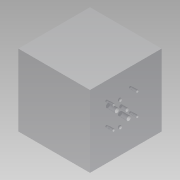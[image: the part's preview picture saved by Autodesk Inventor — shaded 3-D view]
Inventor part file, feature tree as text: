
AUTODESK INVENTOR PART (.ipt)
format: ipt  version: 2014 (Build 180170000, 170)  size: 202,240 bytes
history: native  units: mm
features: other x48, extrude x16, sketch x16
ambient origin geometry x8: Origin, YZ Plane, XZ Plane, XY Plane, X Axis, Y Axis, Z Axis, Center Point
bodies: 实体1 (feature_tree)
feature tree (80):
  extrude  "拉伸1"  Depth=101.0mm
  other  "UCS1"
  other  "UCS2"
  other  "UCS3"
  other  "UCS4"
  other  "UCS5"
  other  "UCS6"
  extrude  "拉伸2"  Depth=125.0mm
  extrude  "拉伸3"  Depth=6.8mm
  extrude  "拉伸4"  Depth=41.3mm
  extrude  "拉伸5"  TaperAngle=0.0deg  [1 undecoded]
  extrude  "拉伸6"  Depth=82.6mm
  extrude  "拉伸7"  TaperAngle=0.0deg  [1 undecoded]
  extrude  "拉伸8"  Depth=8.0mm
  extrude  "拉伸9"  Depth=16.0mm
  extrude  "拉伸10"  Depth=16.0mm
  extrude  "拉伸11"  Depth=16.0mm
  extrude  "拉伸14"  Depth=4.0mm
  extrude  "拉伸15"  Depth=4.0mm
  extrude  "拉伸16"  Depth=4.0mm
  extrude  "拉伸17"  Depth=31.0mm TaperAngle=0.0deg
  extrude  "拉伸18"  Depth=31.0mm
  sketch  "草图1"  dims[d0=250.0mm d1=0.0mm]
  sketch  "草图2"  dims[d2=0.0mm d3=0.0mm d4=0.0mm d5=0.0mm d6=0.0mm d7=0.0mm]
  sketch  "草图3"  dims[d8=0.0mm d9=0.0mm d10=0.0mm d11=0.0mm d12=0.0mm d13=0.0mm]
  sketch  "草图4"  dims[d14=0.0mm d15=0.0mm d16=0.0mm d17=0.0mm d18=0.0mm d19=0.0mm]
  sketch  "草图5"  dims[d20=0.0mm d21=0.0mm d22=0.0mm d23=0.0mm d24=0.0mm d25=0.0mm]
  sketch  "草图6"  dims[d26=0.0mm d27=0.0mm d28=0.0mm d29=0.0mm d30=0.0mm d31=0.0mm]
  sketch  "草图7"  dims[d32=0.0mm d33=0.0mm d34=0.0mm d35=0.0mm d36=0.0mm d37=0.0mm d38=101.0mm]
  sketch  "草图8"  dims[d39=95.0mm d40=125.0mm]
  sketch  "草图9"  dims[d41=124.0mm d44=6.8mm]
  sketch  "草图10"  dims[d45=38.1mm d46=41.3mm]
  sketch  "草图11"  dims[d47=76.2mm d48=0.0mm]
  sketch  "草图15"  dims[d49=76.2mm d50=82.6mm]
  sketch  "草图16"  dims[d51=82.6mm d52=0.0mm]
  sketch  "草图17"  dims[d53=26.0mm d54=0.0mm d55=8.0mm]
  sketch  "草图18"  dims[d56=16.0mm d57=0.0mm d58=16.0mm d59=-10.297443mm]
  sketch  "草图19"  dims[d60=16.0mm d61=-10.297443mm d62=16.0mm d63=-10.297443mm d64=16.0mm d65=-10.297443mm d66=14.7mm d67=54.0mm d68=11.1mm d69=31.0mm d70=0.0mm d71=31.0mm d72=-10.297443mm d73=14.7mm d74=52.4mm d75=9.5mm d76=30.0mm d77=0.0mm d78=30.0mm d79=-10.297443mm d87=11.1mm d88=46.8mm d89=38.0mm d90=22.2mm d91=0.0mm d92=22.2mm d93=-10.297443mm d94=10.4mm d95=23.8mm d96=3.2mm d97=79.4mm d98=23.8mm d99=4.0mm d100=0.0mm d101=4.0mm d102=-10.297443mm d103=4.0mm d104=-8.552113mm]
  other  "UCS1: YZ 平面"
  other  "UCS1: XZ 平面"
  other  "UCS1: XY 平面"
  other  "UCS1: X 轴"
  other  "UCS1: Y 轴"
  other  "UCS1: Z 轴"
  other  "UCS1: 原点"
  other  "UCS2: YZ 平面"
  other  "UCS2: XZ 平面"
  other  "UCS2: XY 平面"
  other  "UCS2: X 轴"
  other  "UCS2: Y 轴"
  other  "UCS2: Z 轴"
  other  "UCS2: 原点"
  other  "UCS3: YZ 平面"
  other  "UCS3: XZ 平面"
  other  "UCS3: XY 平面"
  other  "UCS3: X 轴"
  other  "UCS3: Y 轴"
  other  "UCS3: Z 轴"
  other  "UCS3: 原点"
  other  "UCS4: YZ 平面"
  other  "UCS4: XZ 平面"
  other  "UCS4: XY 平面"
  other  "UCS4: X 轴"
  other  "UCS4: Y 轴"
  other  "UCS4: Z 轴"
  other  "UCS4: 原点"
  other  "UCS5: YZ 平面"
  other  "UCS5: XZ 平面"
  other  "UCS5: XY 平面"
  other  "UCS5: X 轴"
  other  "UCS5: Y 轴"
  other  "UCS5: Z 轴"
  other  "UCS5: 原点"
  other  "UCS6: YZ 平面"
  other  "UCS6: XZ 平面"
  other  "UCS6: XY 平面"
  other  "UCS6: X 轴"
  other  "UCS6: Y 轴"
  other  "UCS6: Z 轴"
  other  "UCS6: 原点"
note: 2 required parameter values undecoded (feature->parameter linkage not recoverable at this tier; creation-order binding heuristic only, values carry confidence <= 0.55)
